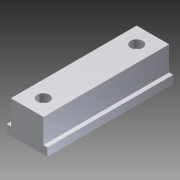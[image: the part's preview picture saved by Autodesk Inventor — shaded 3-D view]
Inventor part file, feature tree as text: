
AUTODESK INVENTOR PART (.ipt)
format: ipt  version: 2012 (Build 160160000, 160)  size: 96,768 bytes
history: native  units: in
note: dims shown in document units (in); Inventor stores cm internally (conversion verified against a paired STEP export)
features: sketch x2, extrude x1, hole x1
ambient origin geometry x8: Origin, YZ Plane, XZ Plane, XY Plane, X Axis, Y Axis, Z Axis, Center Point
bodies: Solid1 (feature_tree)
feature tree (4):
  extrude  "Extrusion1"  Depth=1.0in
  hole  "Hole1"  [1 undecoded]
  sketch  "Sketch1"  dims[d0=1.25in d1=1.0in]
  sketch  "Sketch2"  dims[d2=0.25in d3=0.125in d4=3.875in d5=0.0in d6=0.5in d7=0.5in d8=0.5in d9=0.5in d10=0.25in d11=0.75in d12=0.375in d13=0.25in d14=0.5635in d15=1.0in d16=0.8108in]
note: 1 required parameter value undecoded (feature->parameter linkage not recoverable at this tier; creation-order binding heuristic only, values carry confidence <= 0.55)
